# Revit family: FaEl_CompactResistance
name_source: partatom
category: Fassadenelemente
units: mm (PartAtom-declared; Revit-internal decimal feet)

## family parameters
Beim Laden mit Abzugskörper schneiden = Nein
Gemeinsam genutzt = Nein
Immer vertikal = Ja
OmniClass-Nummer = 23.25.00.00
OmniClass-Titel = Structural and Space Division Products

## types (1)
- FaEl_CompactResistance
    Analytische Konstruktion = <Keine Auswahl>
    Apparent_Density = 1.35 g/cm³
    AssetType = Fixed
    Certification = SEFA
    Combustible = Nein
    Core = Black core
    Duration_Unit = year
    Features = Graffitti-resistant, weather-resistant, flame-retardant core, lightfast, double-hardened, scratch and solvent resistant, easy to clean, custom shapes also available
    Finish_Options = Slabs, triangle, cone, bowl, wave small grey, wave gold large, naturell, letter, bubble, knitter
    FireRating = Euroclass B-s2, d0
    Flexural_Strength = ≥ 90 MPa
    Grade = To BS EN 438-6, Type EDF
    IfcExportAs = IfcCoveringType
    IfcExportType = NOTDEFINED
    IsExternal = Ja
    Manufacturer_Name = FunderMax GmbH
    Manufacturer_URL = http://www.fundermax.at
    Modulus_Of-Elasticity = ≥ 9.0 MPa
    Panel_Material = FunderMax_Compact_Resistance
    Panel_Size_Length = 3660
    Panel_Size_Width = 1630
    Panel_Thickness = 18 mm  [stored 0.0590551 ft]
    Product_Information = https://www.ribaproductselector.com
    Shape = Rectangle
    Size = 3660x1630x0018
    Surface = NT
    Tensile_Strength = ≥ 80 MPa
    Thermal_Conductivity = 0.3 W/mK
    Thermal_Expansion_Coefficient = 18x10^-6 1/K
    Thickness_Options = 4-25 mm
    Tolerances = 0-10 mm to BS EN 438-6
    Version = 3
    Warranty_Duration_Unit = year
    Water_Vapour_Diffusion_Resistance = 17.200 μ

note: [stored X ft] marks values corroborated as IEEE doubles in the binary element streams (Revit-internal decimal feet)
